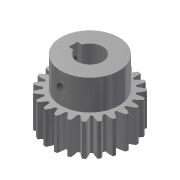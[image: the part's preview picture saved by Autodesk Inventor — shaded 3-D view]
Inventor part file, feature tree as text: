
AUTODESK INVENTOR PART (.ipt)
format: ipt  version: 2018 (Build 220112000, 112)  size: 305,152 bytes
history: native  units: mm (DEFAULTED — no unit token found)
features: sketch x7, extrude x6, plane x5, other x5
ambient origin geometry x8: Origin, YZ Plane, XZ Plane, XY Plane, X Axis, Y Axis, Z Axis, Center Point
bodies: Solid1 (feature_tree)
feature tree (23):
  extrude  "Extrusion1"  Depth=15.0mm TaperAngle=0.0deg
  plane  "Work Plane2"
  plane  "Work Plane8"
  plane  "Work Plane9"
  other  "正齒輪"
  extrude  "擠出2"  Depth=10.0mm TaperAngle=0.0deg
  extrude  "擠出3"  Depth=10.0mm
  extrude  "擠出4"  Depth=10.0mm TaperAngle=0.0deg
  plane  "工作平面11"
  extrude  "擠出5"  TaperAngle=0.0deg  [1 undecoded]
  plane  "工作平面12"
  extrude  "擠出6"  TaperAngle=0.0deg  [1 undecoded]
  other  "螺紋1"
  other  "螺紋2"
  sketch  "Sketch1"  dims[d0=37.5mm d1=15.0mm d2=0.0mm]
  sketch  "Sketch2"  dims[d3=34.5mm d4=10.0mm d5=0.0mm d16=60.0mm d17=0.0mm d34=1.36591mm d39=0.0mm d41=0.0mm d43=60.0mm d46=60.0mm d47=0.0mm d48=0.0mm d49=27.0mm d50=14.0mm d51=0.0mm d52=12.0mm d53=14.0mm d54=0.0mm d56=2.0mm d57=13.8mm d58=14.0mm d59=0.0mm d60=7.0mm d61=4.0mm d62=14.0mm d63=0.0mm d64=7.0mm d65=4.0mm d66=14.0mm d67=0.0mm d68=10.0mm d69=0.0mm d70=10.0mm d71=0.0mm]
  other  "Srf1"
  sketch  "草圖3"
  sketch  "草圖4"
  sketch  "草圖5"
  sketch  "草圖6"
  sketch  "草圖7"
  other  "節圓直徑"
note: 2 required parameter values undecoded (feature->parameter linkage not recoverable at this tier; creation-order binding heuristic only, values carry confidence <= 0.55)
